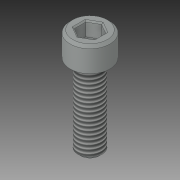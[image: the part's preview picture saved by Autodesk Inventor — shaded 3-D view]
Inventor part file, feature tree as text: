
AUTODESK INVENTOR PART (.ipt)
format: ipt  version: 2018 (Build 220112000, 112)  size: 122,880 bytes
history: native  units: in
note: dims shown in document units (in); Inventor stores cm internally (conversion verified against a paired STEP export)
features: thread x1, imported_body x1
ambient origin geometry x8: Origin, YZ Plane, XZ Plane, XY Plane, X Axis, Y Axis, Z Axis, Center Point
bodies: Solid1 (feature_tree)
feature tree (2):
  thread  "Thread1"  [1 undecoded]
  imported_body  "Imported1"
note: 1 required parameter value undecoded (feature->parameter linkage not recoverable at this tier; creation-order binding heuristic only, values carry confidence <= 0.55)
